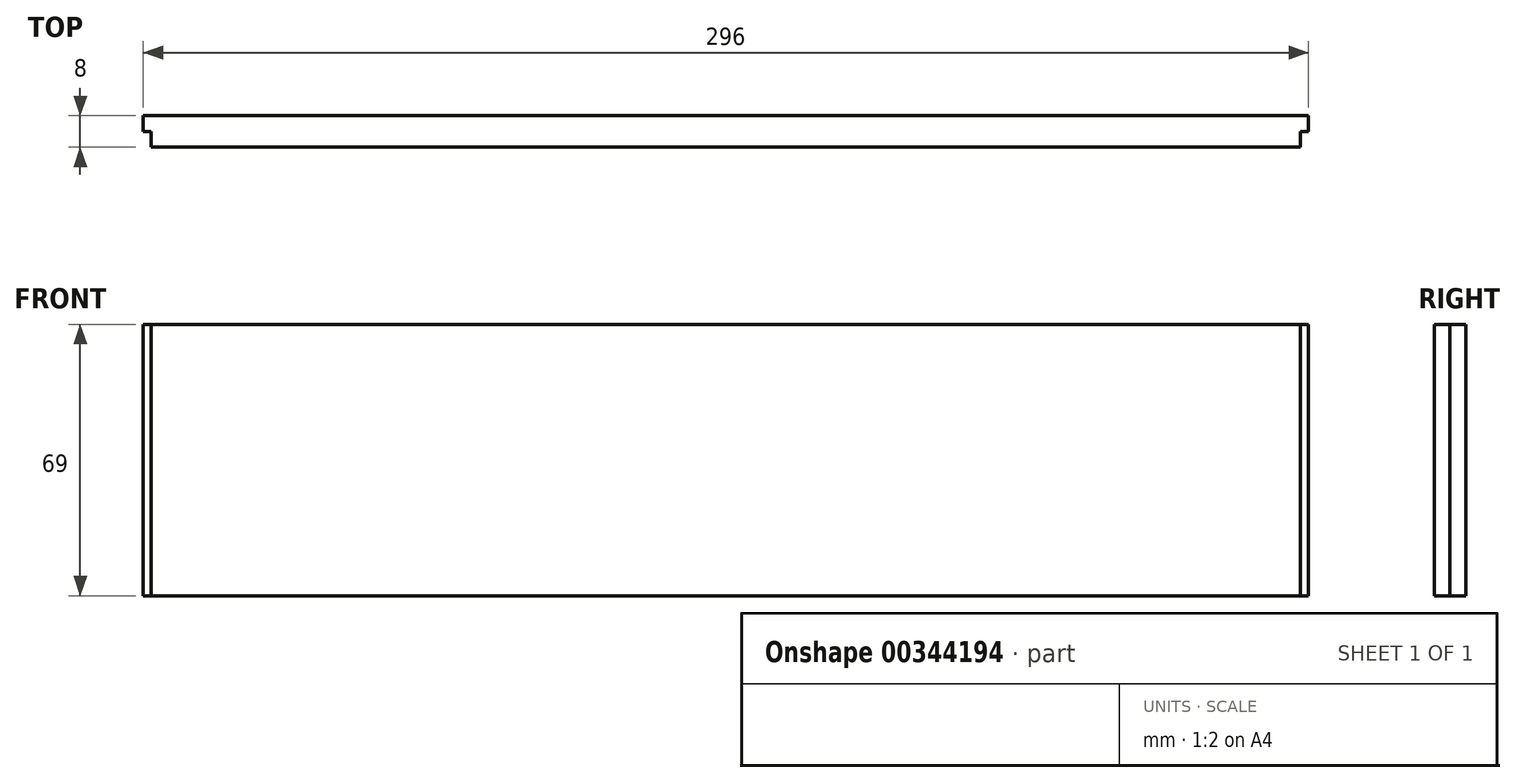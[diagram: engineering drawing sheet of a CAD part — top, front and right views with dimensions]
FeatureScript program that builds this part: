
annotation { "Feature Type Name" : "Feature", "Feature Type Description" : "" }
export const myFeature = defineFeature(function(context is Context, id is Id, definition is map)
    precondition{}
    {
        {
            var Q0;
            Q0=qCreatedBy(makeId("Top.planeOp"),FACE);
            var sketch = newSketch(context, id + "F0", { "sketchPlane" : qUnion([Q0])});
            skLineSegment(sketch, "E0.left", {"start": v(-27.56, -24.4) * mm, "end": v(-27.56, -24.45) * mm});
            skLineSegment(sketch, "E0.right", {"start": v(-26.7, -24.4) * mm, "end": v(-26.7, -24.45) * mm});
            skLineSegment(sketch, "E1.top", {"start": v(-26.7, -28.95) * mm, "end": v(265.3, -28.95) * mm});
            skLineSegment(sketch, "E1.left", {"start": v(-26.7, -24.95) * mm, "end": v(-26.7, -28.95) * mm});
            skLineSegment(sketch, "E1.right", {"start": v(265.3, -24.95) * mm, "end": v(265.3, -28.95) * mm});
            skLineSegment(sketch, "E2.bottom", {"start": v(267.3, -24.95) * mm, "end": v(265.3, -24.95) * mm});
            skLineSegment(sketch, "E2.top", {"start": v(267.3, -20.95) * mm, "end": v(-28.7, -20.95) * mm});
            skLineSegment(sketch, "E2.left", {"start": v(267.3, -24.95) * mm, "end": v(267.3, -20.95) * mm});
            skLineSegment(sketch, "E2.right", {"start": v(-28.7, -24.95) * mm, "end": v(-28.7, -20.95) * mm});
            skLineSegment(sketch, "E3.trimOffspring", {"start": v(-26.7, -24.95) * mm, "end": v(-28.7, -24.95) * mm});
            skSolve(sketch);
        }
        {
            var Q0;
            Q0 = qSketchRegion(id + "F0", true);
            extrude(context, id + "F1", {"entities" : qUnion([Q0]), "depth" : 69 * mm});
        }
    });
